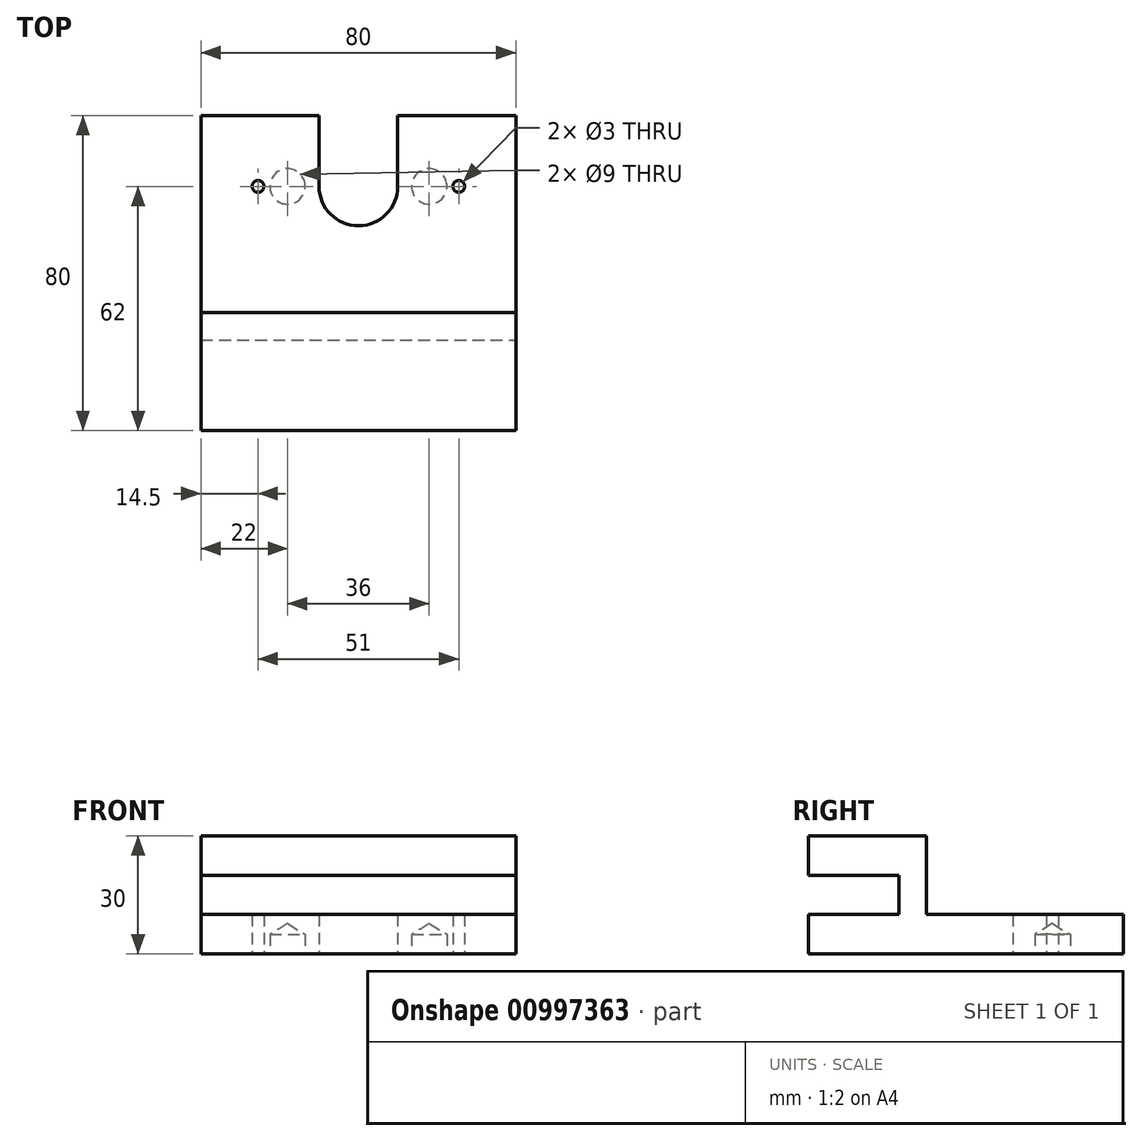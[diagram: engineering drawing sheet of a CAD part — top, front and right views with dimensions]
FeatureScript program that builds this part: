
annotation { "Feature Type Name" : "Feature", "Feature Type Description" : "" }
export const myFeature = defineFeature(function(context is Context, id is Id, definition is map)
    precondition{}
    {
        {
            var Q0;
            Q0=qCreatedBy(makeId("Top.planeOp"),FACE);
            var sketch = newSketch(context, id + "F0", { "sketchPlane" : qUnion([Q0])});
            skLineSegment(sketch, "E0.bottom", {"start": v(40, -40) * mm, "end": v(-40, -40) * mm});
            skLineSegment(sketch, "E0.top", {"start": v(40, 40) * mm, "end": v(10, 40) * mm});
            skLineSegment(sketch, "E0.left", {"start": v(40, -40) * mm, "end": v(40, 40) * mm});
            skLineSegment(sketch, "E0.right", {"start": v(-40, -40) * mm, "end": v(-40, 40) * mm});
            skPoint(sketch, "E0.middle", {"position": v(0, 0) * mm});
            skLineSegment(sketch, "E1.MirrorCS", {"start": v(-40, 40) * mm, "end": v(-10, 40) * mm});
            skLineSegment(sketch, "E2", {"start": v(10, 40) * mm, "end": v(10, 22) * mm});
            skLineSegment(sketch, "E3.MirrorCS", {"start": v(-10, 40) * mm, "end": v(-10, 22) * mm});
            skArc(sketch, "E4", {"start": v(-10, 22) * mm, "mid": v(0, 12) * mm, "end": v(10, 22) * mm});
            skPoint(sketch, "E5", {"position": v(25.5, 22) * mm});
            skPoint(sketch, "E6.MirrorP", {"position": v(-25.5, 22) * mm});
            skPoint(sketch, "E7", {"position": v(18, 22) * mm});
            skPoint(sketch, "E8.MirrorP", {"position": v(-18, 22) * mm});
            skSolve(sketch);
        }
        {
            var Q0;
            Q0 = qSketchRegion(id + "F0", true);
            extrude(context, id + "F1", {"entities" : qUnion([Q0]), "depth" : 10 * mm, "offsetDistance" : 25 * mm});
        }
        {
            var Q0;
            Q0=makeQuery(id+"F1.opExtrude","CAP_FACE",FACE,{"disambiguationData":[OSD([sQuery(id+"F0.wireOp",EDGE,"E0.bottom"),sQuery(id+"F0.wireOp",EDGE,"E0.top"),sQuery(id+"F0.wireOp",EDGE,"E0.left"),sQuery(id+"F0.wireOp",EDGE,"E0.right"),sQuery(id+"F0.wireOp",EDGE,"E1.MirrorCS"),sQuery(id+"F0.wireOp",EDGE,"E2"),sQuery(id+"F0.wireOp",EDGE,"E3.MirrorCS"),sQuery(id+"F0.wireOp",EDGE,"E4"),sQuery(id+"F0.wireOp",EDGE,"KVbkiZfB-H6Du-TPPV-6q8I-uf0WxIEjbF18"),sQuery(id+"F0.wireOp",EDGE,"1c7917fc-9461-4d3b-b9cc-c5de14806d1c0.MirrorC")])],"isStart":false});
            var sketch = newSketch(context, id + "F2", { "sketchPlane" : qUnion([Q0])});
            skLineSegment(sketch, "E9.bottom", {"start": v(-40, -10) * mm, "end": v(40, -10) * mm});
            skLineSegment(sketch, "E9.top", {"start": v(-40, -17) * mm, "end": v(40, -17) * mm});
            skLineSegment(sketch, "E9.left", {"start": v(-40, -10) * mm, "end": v(-40, -17) * mm});
            skLineSegment(sketch, "E9.right", {"start": v(40, -10) * mm, "end": v(40, -17) * mm});
            skSolve(sketch);
        }
        {
            var Q0;
            Q0 = qSketchRegion(id + "F2", true);
            extrude(context, id + "F3", {"entities" : qUnion([Q0]), "operationType" : NewBodyOperationType.ADD, "depth" : 20 * mm, "offsetDistance" : 25 * mm});
        }
        {
            var Q0;
            Q0=makeQuery(id+"F3.opExtrude","SWEPT_FACE",FACE,{"disambiguationData":[OSD([sQuery(id+"F2.wireOp",EDGE,"E9.top")])]});
            var sketch = newSketch(context, id + "F4", { "sketchPlane" : qUnion([Q0])});
            skLineSegment(sketch, "E10.bottom", {"start": v(-40, 30) * mm, "end": v(40, 30) * mm});
            skLineSegment(sketch, "E10.top", {"start": v(-40, 20) * mm, "end": v(40, 20) * mm});
            skLineSegment(sketch, "E10.left", {"start": v(-40, 30) * mm, "end": v(-40, 20) * mm});
            skLineSegment(sketch, "E10.right", {"start": v(40, 30) * mm, "end": v(40, 20) * mm});
            skSolve(sketch);
        }
        {
            var Q0;
            Q0 = qSketchRegion(id + "F4", true);
            extrude(context, id + "F5", {"entities" : qUnion([Q0]), "operationType" : NewBodyOperationType.ADD, "depth" : 23 * mm, "offsetDistance" : 25 * mm});
        }
        {
            var Q0;
            Q0=sQuery(id+"F0.wireOp",VERTEX,"E5");
            var Q1;
            Q1=makeQuery(id+"F1.opExtrude","SWEPT_BODY",BODY,{"disambiguationData":[OSD([sQuery(id+"F0.wireOp",EDGE,"E0.bottom"),sQuery(id+"F0.wireOp",EDGE,"E0.top"),sQuery(id+"F0.wireOp",EDGE,"E0.left"),sQuery(id+"F0.wireOp",EDGE,"E0.right"),sQuery(id+"F0.wireOp",EDGE,"E1.MirrorCS"),sQuery(id+"F0.wireOp",EDGE,"E2"),sQuery(id+"F0.wireOp",EDGE,"E3.MirrorCS"),sQuery(id+"F0.wireOp",EDGE,"E4")])]});
            hole(context, id + "F6", {"style" : HoleStyle.SIMPLE, "endStyle" : HoleEndStyle.THROUGH, "oppositeDirection" : true, "holeDiameter" : 3 * mm, "majorDiameter" : 5 * mm, "isTappedThrough" : true, "tappedDepth" : 12 * mm, "tapClearance" : 3, "locations" : qUnion([Q0]), "scope" : qUnion([Q1])});
        }
        {
            var Q0;
            Q0=sQuery(id+"F0.wireOp",VERTEX,"E6.MirrorP");
            var Q1;
            Q1=makeQuery(id+"F1.opExtrude","SWEPT_BODY",BODY,{"disambiguationData":[OSD([sQuery(id+"F0.wireOp",EDGE,"E0.bottom"),sQuery(id+"F0.wireOp",EDGE,"E0.top"),sQuery(id+"F0.wireOp",EDGE,"E0.left"),sQuery(id+"F0.wireOp",EDGE,"E0.right"),sQuery(id+"F0.wireOp",EDGE,"E1.MirrorCS"),sQuery(id+"F0.wireOp",EDGE,"E2"),sQuery(id+"F0.wireOp",EDGE,"E3.MirrorCS"),sQuery(id+"F0.wireOp",EDGE,"E4")])]});
            hole(context, id + "F7", {"style" : HoleStyle.SIMPLE, "endStyle" : HoleEndStyle.THROUGH, "oppositeDirection" : true, "holeDiameter" : 3 * mm, "majorDiameter" : 5 * mm, "isTappedThrough" : true, "tappedDepth" : 12 * mm, "tapClearance" : 3, "locations" : qUnion([Q0]), "scope" : qUnion([Q1])});
        }
        {
            var Q0;
            Q0=sQuery(id+"F0.wireOp",VERTEX,"E7");
            var Q1;
            Q1=sQuery(id+"F0.wireOp",VERTEX,"E8.MirrorP");
            var Q2;
            Q2=makeQuery(id+"F1.opExtrude","SWEPT_BODY",BODY,{"disambiguationData":[OSD([sQuery(id+"F0.wireOp",EDGE,"E0.bottom"),sQuery(id+"F0.wireOp",EDGE,"E0.top"),sQuery(id+"F0.wireOp",EDGE,"E0.left"),sQuery(id+"F0.wireOp",EDGE,"E0.right"),sQuery(id+"F0.wireOp",EDGE,"E1.MirrorCS"),sQuery(id+"F0.wireOp",EDGE,"E2"),sQuery(id+"F0.wireOp",EDGE,"E3.MirrorCS"),sQuery(id+"F0.wireOp",EDGE,"E4")])]});
            hole(context, id + "F8", {"style" : HoleStyle.SIMPLE, "endStyle" : HoleEndStyle.BLIND, "oppositeDirection" : true, "holeDiameter" : 9 * mm, "majorDiameter" : 5 * mm, "holeDepth" : 5 * mm, "isTappedThrough" : true, "tappedDepth" : 12 * mm, "tapClearance" : 3, "startFromSketch" : true, "locations" : qUnion([Q0, Q1]), "scope" : qUnion([Q2])});
        }
    });
